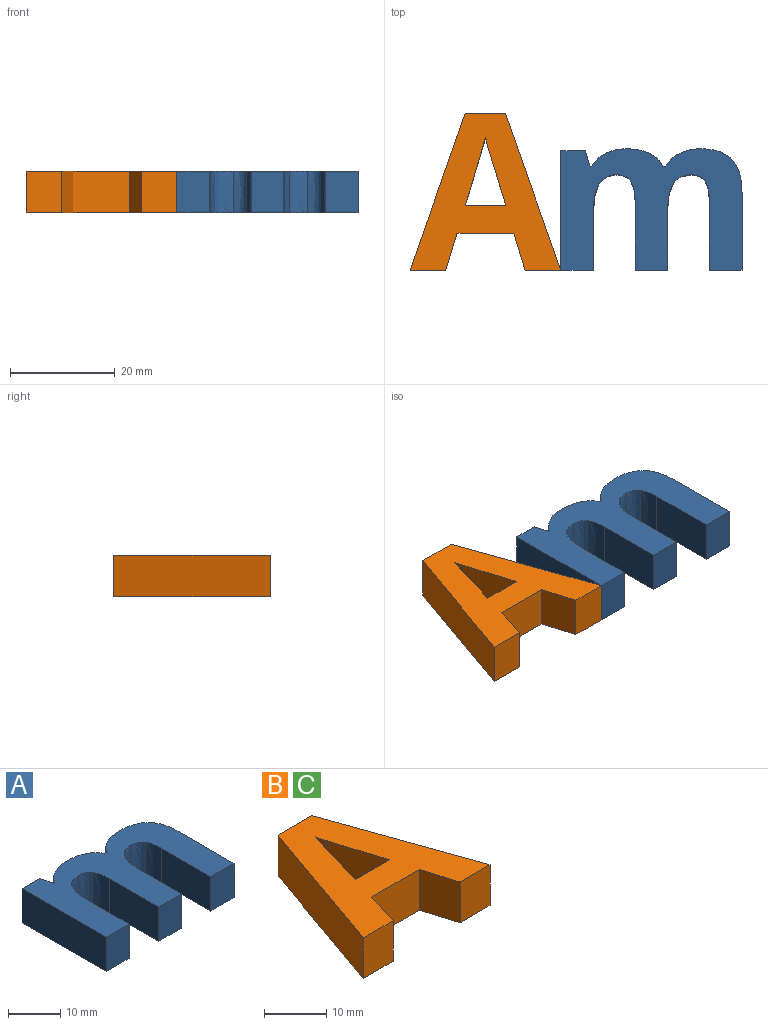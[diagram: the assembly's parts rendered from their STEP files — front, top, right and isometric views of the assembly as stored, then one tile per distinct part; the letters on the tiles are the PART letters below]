
ASSEMBLY  parts=3 mates=1
PART A: 30 faces, bbox 34.5x23.2x8 mm
  f0: plane 8x6.2mm, normal (0,-1,0), area 49.6mm2, adj f1,f27,f28,f29
  f1: plane 11.41x8mm, normal (1,0,0), area 91.3mm2, adj f0,f2,f28,f29
  f2: extruded ~8x5.17mm, area 42.9mm2, adj f1,f3,f28,f29
  f3: extruded ~8x3.41mm, area 31.5mm2, adj f2,f4,f28,f29
  f4: extruded ~8x2.59mm, area 24mm2, adj f3,f5,f28,f29
  f5: extruded ~8x3.69mm, area 30.7mm2, adj f4,f6,f28,f29
  f6: plane 13.29x8mm, normal (-1,0,0), area 106.3mm2, adj f5,f7,f28,f29
  f7: plane 8x6.22mm, normal (0,-1,0), area 49.8mm2, adj f6,f8,f28,f29
  f8: plane 14.83x8mm, normal (1,0,0), area 118.6mm2, adj f7,f9,f28,f29
  f9: extruded ~8x6.36mm, area 54.7mm2, adj f8,f10,f28,f29
  f10: extruded ~8x5.85mm, area 50.7mm2, adj f9,f11,f28,f29
  f11: extruded ~8x4.02mm, area 33.2mm2, adj f10,f12,f28,f29
  f12: extruded ~8x2.7mm, area 29.6mm2, adj f11,f13,f28,f29
  f13: plane 8x0.55mm, normal (0,1,0), area 4.4mm2, adj f12,f14,f28,f29
  f14: extruded ~8x6.92mm, area 64.8mm2, adj f13,f15,f28,f29
  f15: extruded ~8x3.97mm, area 32.8mm2, adj f14,f16,f28,f29
  f16: extruded ~8x2.65mm, area 29.3mm2, adj f15,f17,f28,f29
  f17: plane 8x0.35mm, normal (0,1,0), area 2.8mm2, adj f16,f18,f28,f29
  f18: plane 8x2.91mm, normal (0.96,0.28,0), area 24.2mm2, adj f17,f19,f28,f29
  f19: plane 8x4.74mm, normal (0,1,0), area 37.9mm2, adj f18,f20,f28,f29
  f20: plane 22.75x8mm, normal (-1,0,0), area 182mm2, adj f19,f21,f28,f29
  f21: plane 8x6.2mm, normal (0,-1,0), area 49.6mm2, adj f20,f22,f28,f29
  f22: plane 10.7x8mm, normal (1,0,0), area 85.6mm2, adj f21,f23,f28,f29
  f23: extruded ~8x5.76mm, area 47.4mm2, adj f22,f24,f28,f29
  f24: extruded ~8x3.46mm, area 32.6mm2, adj f23,f25,f28,f29
  f25: extruded ~8x2.59mm, area 24mm2, adj f24,f26,f28,f29
  f26: extruded ~8x3.69mm, area 30.7mm2, adj f25,f27,f28,f29
  f27: plane 13.29x8mm, normal (-1,0,0), area 106.3mm2, adj f0,f26,f28,f29
  f28: plane 34.54x23.17mm, normal (0,0,1), area 491.2mm2, adj f0,f1,f2,f3,f4,f5,f6,f7
  f29: plane 34.54x23.17mm, normal (0,0,-1), area 491.2mm2, adj f0,f1,f2,f3,f4,f5,f6,f7
PART B: 14 faces, bbox 28.8x29.9x8 mm
  f0: extruded ~10.89x8mm, area 91.2mm2, adj f1,f11,f12,f13
  f1: plane 8x7.75mm, normal (0,1,0), area 62mm2, adj f0,f2,f12,f13
  f2: extruded ~12.88x8mm, area 107.5mm2, adj f1,f11,f12,f13
  f3: plane 8x7.08mm, normal (-0.96,-0.29,0), area 59.2mm2, adj f4,f10,f12,f13
  f4: plane 8x6.8mm, normal (0,-1,0), area 54.4mm2, adj f3,f5,f12,f13
  f5: plane 29.87x10.54mm, normal (0.94,0.33,0), area 253.4mm2, adj f4,f6,f12,f13
  f6: plane 8x7.71mm, normal (0,1,0), area 61.7mm2, adj f5,f7,f12,f13
  f7: plane 29.87x10.5mm, normal (-0.94,0.33,0), area 253.3mm2, adj f6,f8,f12,f13
  f8: plane 8x6.8mm, normal (0,-1,0), area 54.4mm2, adj f7,f9,f12,f13
  f9: plane 8x7.08mm, normal (0.96,-0.29,0), area 59.2mm2, adj f8,f10,f12,f13
  f10: plane 10.85x8mm, normal (0,-1,0), area 86.8mm2, adj f3,f9,f12,f13
  f11: extruded ~8x1.99mm, area 16.5mm2, adj f0,f2,f12,f13
  f12: plane 29.87x28.75mm, normal (0,0,1), area 403.5mm2, adj f0,f1,f2,f3,f4,f5,f6,f7
  f13: plane 29.87x28.75mm, normal (0,0,-1), area 403.5mm2, adj f0,f1,f2,f3,f4,f5,f6,f7
PART C: same geometry as B
PLACE A t=(-4.31,-3.93,6.12)mm
PLACE B t=(-1.06,-3.93,6.12)mm
PLACE C t=(-1.06,-3.93,6.12)mm fixed
MATE fastened A.f21 <-> C.f4  axis (0,-1,0) through (-44.92,-18.93,6.12)mm
